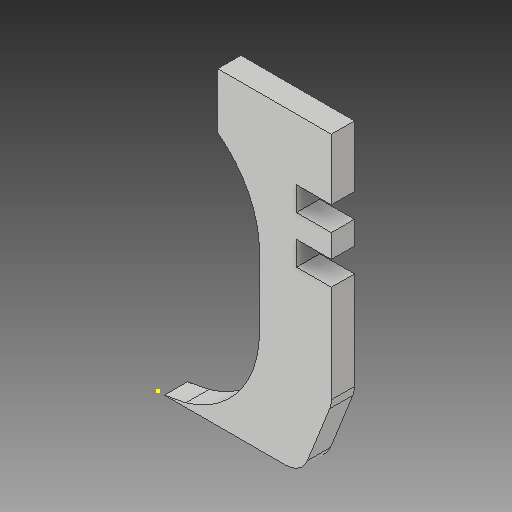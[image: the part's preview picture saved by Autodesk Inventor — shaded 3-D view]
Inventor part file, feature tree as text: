
AUTODESK INVENTOR PART (.ipt)
format: ipt  version: 2017 (Build 210142000, 142)  size: 116,736 bytes
history: native  units: in
note: dims shown in document units (in); Inventor stores cm internally (conversion verified against a paired STEP export)
features: sketch x4, other x3
ambient origin geometry x8: Origin, YZ Plane, XZ Plane, XY Plane, X Axis, Y Axis, Z Axis, Center Point
bodies: Solid1 (feature_tree)
feature tree (7):
  other  "Finger.ipt"
  other  "Solid1::Finger.ipt"
  other  "TaggingFeature1"
  sketch  "Sketch1"  dims[d0=0.3937in]
  sketch  "Sketch2"
  sketch  "Sketch3"
  sketch  "Sketch4"
